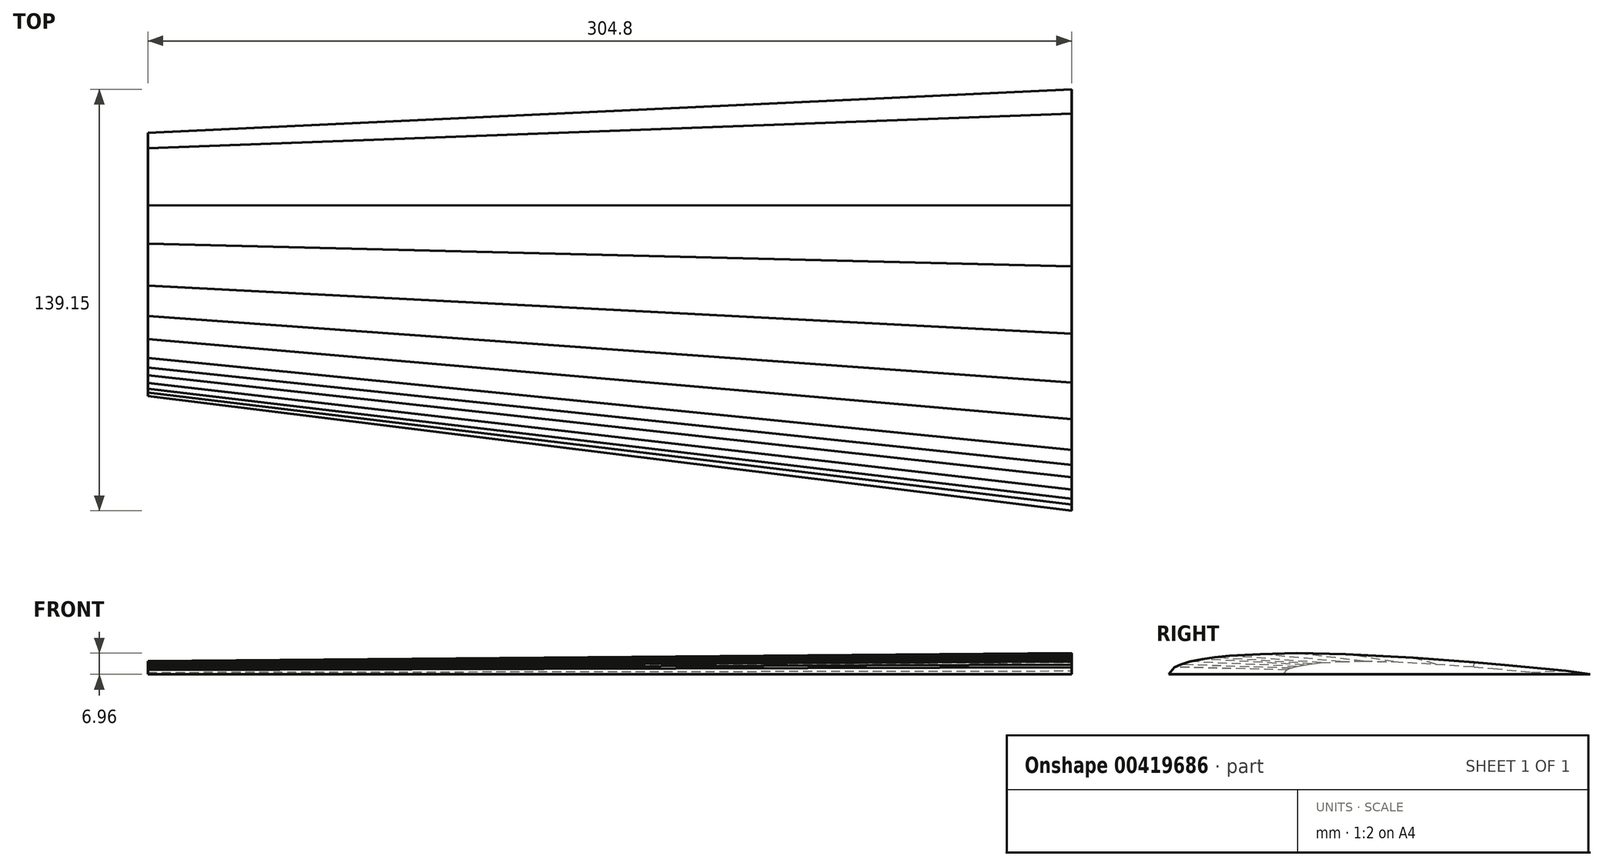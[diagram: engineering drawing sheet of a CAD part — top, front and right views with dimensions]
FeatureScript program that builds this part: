
annotation { "Feature Type Name" : "Feature", "Feature Type Description" : "" }
export const myFeature = defineFeature(function(context is Context, id is Id, definition is map)
    precondition{}
    {
        {
            var Q0;
            Q0=qCreatedBy(makeId("Right.planeOp"),FACE);
            cPlane(context, id + "F0", {"entities" : qUnion([Q0]), "cplaneType" : CPlaneType.OFFSET, "offset" : 228.6 * mm, "width" : 152.4 * mm, "height" : 152.4 * mm});
        }
        {
            var Q0;
            Q0=qCreatedBy(id+"F0.planeOp",FACE);
            cPlane(context, id + "F1", {"entities" : qUnion([Q0]), "cplaneType" : CPlaneType.OFFSET, "offset" : 304.8 * mm, "width" : 152.4 * mm, "height" : 152.4 * mm});
        }
        {
            var Q0;
            Q0=qCreatedBy(id+"F0.planeOp",FACE);
            var sketch = newSketch(context, id + "F2", { "sketchPlane" : qUnion([Q0])});
            skLineSegment(sketch, "E0", {"start": v(74.22, 0) * mm, "end": v(-12.7, 0) * mm});
            skPoint(sketch, "E1.MirrorP", {"position": v(-12.7, 0) * mm});
            skLineSegment(sketch, "E2.MirrorCS", {"start": v(-12.7, 0) * mm, "end": v(-11.45, 1.48) * mm});
            skLineSegment(sketch, "E3.MirrorCS", {"start": v(-5.78, 3.13) * mm, "end": v(-3.26, 3.48) * mm});
            skLineSegment(sketch, "E4.MirrorCS", {"start": v(-3.26, 3.48) * mm, "end": v(-0.1, 3.82) * mm});
            skLineSegment(sketch, "E5.MirrorCS", {"start": v(-8.3, 2.6) * mm, "end": v(-5.78, 3.13) * mm});
            skLineSegment(sketch, "E6.MirrorCS", {"start": v(-10.2, 2) * mm, "end": v(-8.3, 2.6) * mm});
            skLineSegment(sketch, "E7.MirrorCS", {"start": v(-10.2, 2) * mm, "end": v(-11.45, 1.48) * mm});
            skLineSegment(sketch, "E8.MirrorCS", {"start": v(69.17, 0.7) * mm, "end": v(74.22, 0) * mm});
            skLineSegment(sketch, "E9.MirrorCS", {"start": v(50.28, 2.48) * mm, "end": v(56.58, 1.91) * mm});
            skLineSegment(sketch, "E10.MirrorCS", {"start": v(37.68, 3.39) * mm, "end": v(50.28, 2.48) * mm});
            skLineSegment(sketch, "E11.MirrorCS", {"start": v(23.83, 4.17) * mm, "end": v(37.68, 3.39) * mm});
            skLineSegment(sketch, "E12.MirrorCS", {"start": v(56.58, 1.91) * mm, "end": v(69.17, 0.7) * mm});
            skLineSegment(sketch, "E13.MirrorCS", {"start": v(13.75, 4.35) * mm, "end": v(23.83, 4.17) * mm});
            skLineSegment(sketch, "E14.MirrorCS", {"start": v(6.18, 4.17) * mm, "end": v(13.75, 4.35) * mm});
            skLineSegment(sketch, "E15.MirrorCS", {"start": v(-0.1, 3.82) * mm, "end": v(6.18, 4.17) * mm});
            skSolve(sketch);
        }
        {
            var Q0;
            Q0=qCreatedBy(id+"F1.planeOp",FACE);
            var sketch = newSketch(context, id + "F3", { "sketchPlane" : qUnion([Q0])});
            skLineSegment(sketch, "E16", {"start": v(-50.53, 0) * mm, "end": v(88.62, 0) * mm});
            skLineSegment(sketch, "E17.MirrorCS", {"start": v(-46.5, 3.2) * mm, "end": v(-43.47, 4.17) * mm});
            skLineSegment(sketch, "E18.MirrorCS", {"start": v(-46.5, 3.2) * mm, "end": v(-48.52, 2.37) * mm});
            skLineSegment(sketch, "E19.MirrorCS", {"start": v(-43.47, 4.17) * mm, "end": v(-39.44, 5) * mm});
            skLineSegment(sketch, "E20.MirrorCS", {"start": v(-39.44, 5) * mm, "end": v(-35.41, 5.57) * mm});
            skLineSegment(sketch, "E21.MirrorCS", {"start": v(-50.53, 0) * mm, "end": v(-48.52, 2.37) * mm});
            skLineSegment(sketch, "E22.MirrorCS", {"start": v(-35.41, 5.57) * mm, "end": v(-30.36, 6.12) * mm});
            skLineSegment(sketch, "E23.MirrorCS", {"start": v(80.55, 1.11) * mm, "end": v(88.62, 0) * mm});
            skLineSegment(sketch, "E24.MirrorCS", {"start": v(60.38, 3.06) * mm, "end": v(80.55, 1.11) * mm});
            skLineSegment(sketch, "E25.MirrorCS", {"start": v(50.3, 3.97) * mm, "end": v(60.38, 3.06) * mm});
            skLineSegment(sketch, "E26.MirrorCS", {"start": v(30.14, 5.43) * mm, "end": v(50.3, 3.97) * mm});
            skLineSegment(sketch, "E27.MirrorCS", {"start": v(7.95, 6.68) * mm, "end": v(30.14, 5.43) * mm});
            skLineSegment(sketch, "E28.MirrorCS", {"start": v(-8.18, 6.96) * mm, "end": v(7.95, 6.68) * mm});
            skLineSegment(sketch, "E29.MirrorCS", {"start": v(-20.29, 6.68) * mm, "end": v(-8.18, 6.96) * mm});
            skLineSegment(sketch, "E30.MirrorCS", {"start": v(-30.36, 6.12) * mm, "end": v(-20.29, 6.68) * mm});
            skSolve(sketch);
        }
        {
            var Q0;
            Q0 = qSketchRegion(id + "F2", true);
            var Q1;
            Q1 = qSketchRegion(id + "F3", true);
            loft(context, id + "F4", {"sheetProfilesArray" : [{ "sheetProfileEntities" : qUnion([Q0]) }, { "sheetProfileEntities" : qUnion([Q1]) }]});
        }
    });
